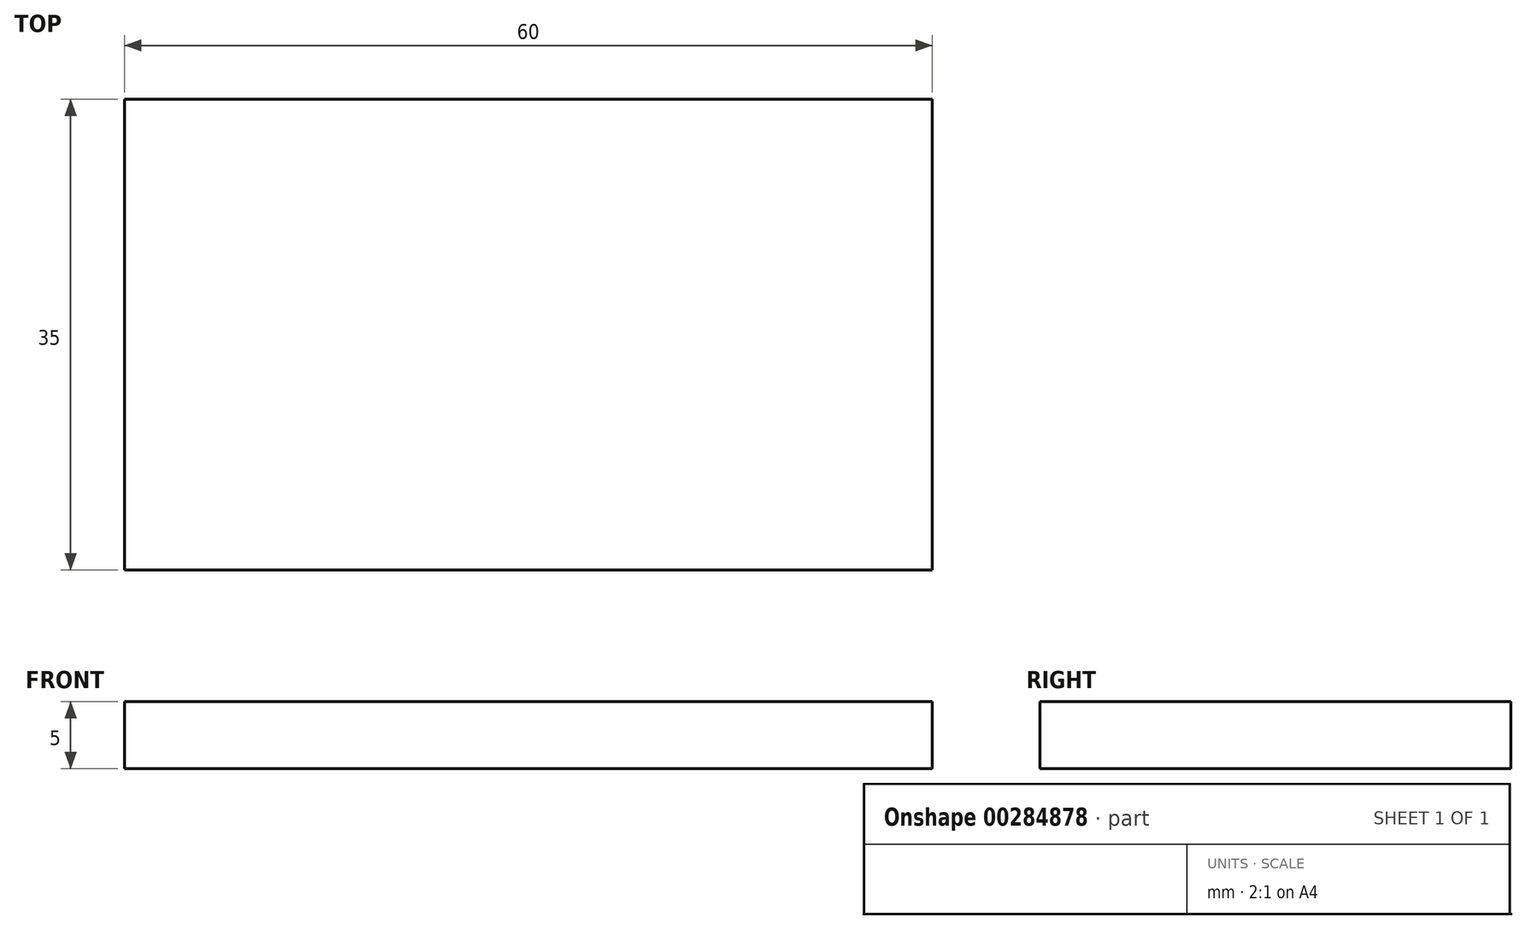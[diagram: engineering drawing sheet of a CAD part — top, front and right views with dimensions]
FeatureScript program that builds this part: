
annotation { "Feature Type Name" : "Feature", "Feature Type Description" : "" }
export const myFeature = defineFeature(function(context is Context, id is Id, definition is map)
    precondition{}
    {
        {
            var Q0;
            Q0=qCreatedBy(makeId("Top.planeOp"),FACE);
            var sketch = newSketch(context, id + "F0", { "sketchPlane" : qUnion([Q0])});
            skLineSegment(sketch, "E0.bottom", {"start": v(30, 17.5) * mm, "end": v(-30, 17.5) * mm});
            skLineSegment(sketch, "E0.top", {"start": v(30, -17.5) * mm, "end": v(-30, -17.5) * mm});
            skLineSegment(sketch, "E0.left", {"start": v(30, 17.5) * mm, "end": v(30, -17.5) * mm});
            skLineSegment(sketch, "E0.right", {"start": v(-30, 17.5) * mm, "end": v(-30, -17.5) * mm});
            skPoint(sketch, "E0.middle", {"position": v(0, 0) * mm});
            skSolve(sketch);
        }
        {
            var Q0;
            Q0 = qSketchRegion(id + "F0", true);
            extrude(context, id + "F1", {"entities" : qUnion([Q0]), "depth" : 5 * mm});
        }
    });
